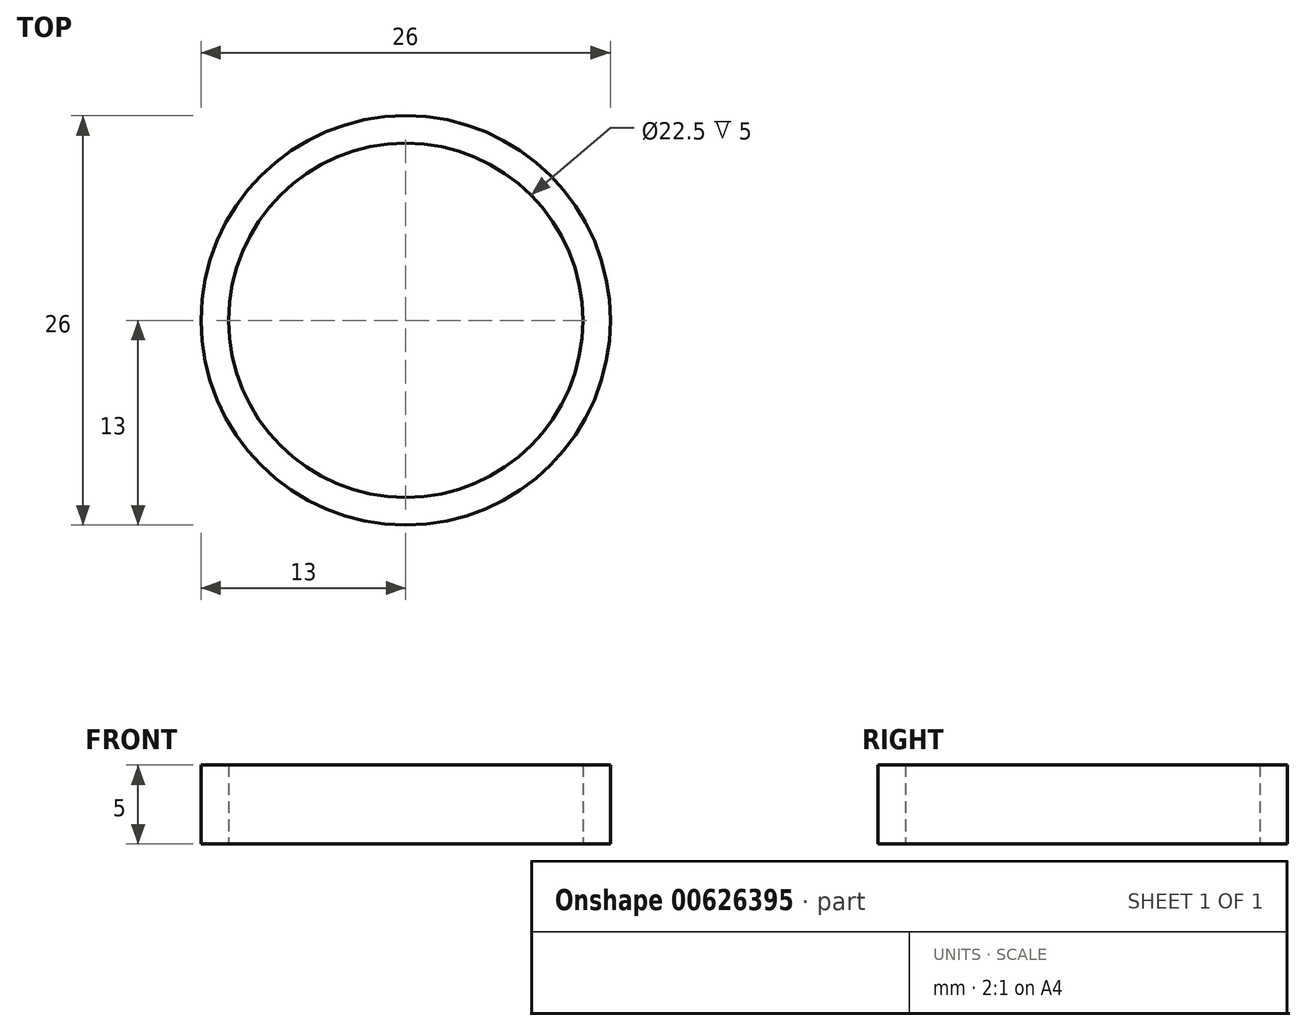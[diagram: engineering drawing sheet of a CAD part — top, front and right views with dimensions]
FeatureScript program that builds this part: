
annotation { "Feature Type Name" : "Feature", "Feature Type Description" : "" }
export const myFeature = defineFeature(function(context is Context, id is Id, definition is map)
    precondition{}
    {
        {
            var Q0;
            Q0=qCreatedBy(makeId("Top.planeOp"),FACE);
            var sketch = newSketch(context, id + "F0", { "sketchPlane" : qUnion([Q0])});
            skCircle(sketch, "E0", {"center": v(0, 0) * mm, "radius": 11.25 * mm});
            skCircle(sketch, "E1", {"center": v(0, 0) * mm, "radius": 13 * mm});
            skSolve(sketch);
        }
        {
            var Q0;
            Q0 = qSketchRegion(id + "F0", true);
            extrude(context, id + "F1", {"entities" : qUnion([Q0]), "depth" : 5 * mm, "offsetDistance" : 25 * mm});
        }
    });
